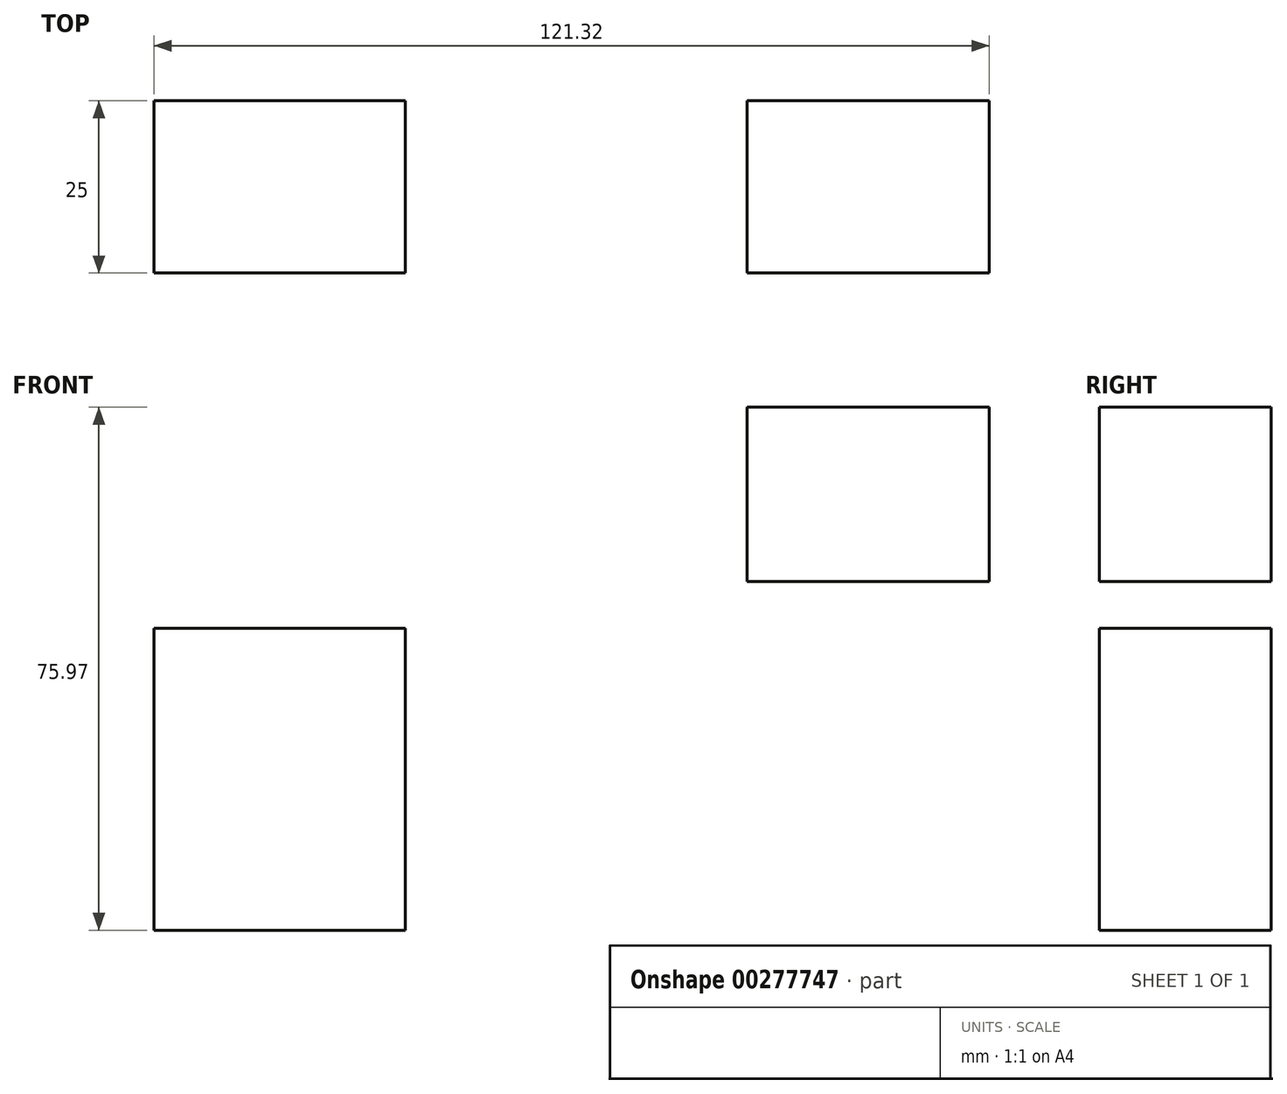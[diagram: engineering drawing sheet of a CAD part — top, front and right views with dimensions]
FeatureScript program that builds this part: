
annotation { "Feature Type Name" : "Feature", "Feature Type Description" : "" }
export const myFeature = defineFeature(function(context is Context, id is Id, definition is map)
    precondition{}
    {
        {
            var Q0;
            Q0=qCreatedBy(makeId("Front.planeOp"),FACE);
            var sketch = newSketch(context, id + "F0", { "sketchPlane" : qUnion([Q0])});
            skLineSegment(sketch, "E0.bottom", {"start": v(-82.07, -26.42) * mm, "end": v(-118.61, -26.42) * mm});
            skLineSegment(sketch, "E0.top", {"start": v(-82.07, 17.43) * mm, "end": v(-118.61, 17.43) * mm});
            skLineSegment(sketch, "E0.left", {"start": v(-82.07, -26.42) * mm, "end": v(-82.07, 17.43) * mm});
            skLineSegment(sketch, "E0.right", {"start": v(-118.61, -26.42) * mm, "end": v(-118.61, 17.43) * mm});
            skPoint(sketch, "E0.middle", {"position": v(-100.34, -4.5) * mm});
            skLineSegment(sketch, "E1.bottom", {"start": v(-32.42, 24.25) * mm, "end": v(2.7, 24.25) * mm});
            skLineSegment(sketch, "E1.top", {"start": v(-32.42, 49.55) * mm, "end": v(2.7, 49.55) * mm});
            skLineSegment(sketch, "E1.left", {"start": v(-32.42, 24.25) * mm, "end": v(-32.42, 49.55) * mm});
            skLineSegment(sketch, "E1.right", {"start": v(2.7, 24.25) * mm, "end": v(2.7, 49.55) * mm});
            skPoint(sketch, "E1.middle", {"position": v(-14.86, 36.9) * mm});
            skSolve(sketch);
        }
        {
            var Q0;
            Q0=makeQuery(id+"F0.imprint","IMPRINT",FACE,{"disambiguationData":[TD([[makeQuery(id+"F0.imprint","IMPRINT",EDGE,{"derivedFrom":sQuery(id+"F0.wireOp",EDGE,"E0.bottom")}),-1.0]])]});
            var Q1;
            Q1=makeQuery(id+"F0.imprint","IMPRINT",FACE,{"disambiguationData":[TD([[makeQuery(id+"F0.imprint","IMPRINT",EDGE,{"derivedFrom":sQuery(id+"F0.wireOp",EDGE,"E1.bottom")}),1.0]])]});
            var Q2;
            Q2=sQuery(id+"F0.wireOp",EDGE,"E0.top");
            var Q3;
            Q3=sQuery(id+"F0.wireOp",EDGE,"E0.bottom");
            var Q4;
            Q4=sQuery(id+"F0.wireOp",EDGE,"E1.left");
            var Q5;
            Q5=sQuery(id+"F0.wireOp",EDGE,"E0.left");
            var Q6;
            Q6=sQuery(id+"F0.wireOp",EDGE,"E0.right");
            var Q7;
            Q7=sQuery(id+"F0.wireOp",EDGE,"E1.right");
            var Q8;
            Q8=sQuery(id+"F0.wireOp",EDGE,"E1.bottom");
            var Q9;
            Q9=sQuery(id+"F0.wireOp",EDGE,"E1.top");
            extrude(context, id + "F1", {"entities" : qUnion([Q0, Q1]), "surfaceEntities" : qUnion([Q2, Q3, Q4, Q5, Q6, Q7, Q8, Q9]), "depth" : 25 * mm});
        }
    });
